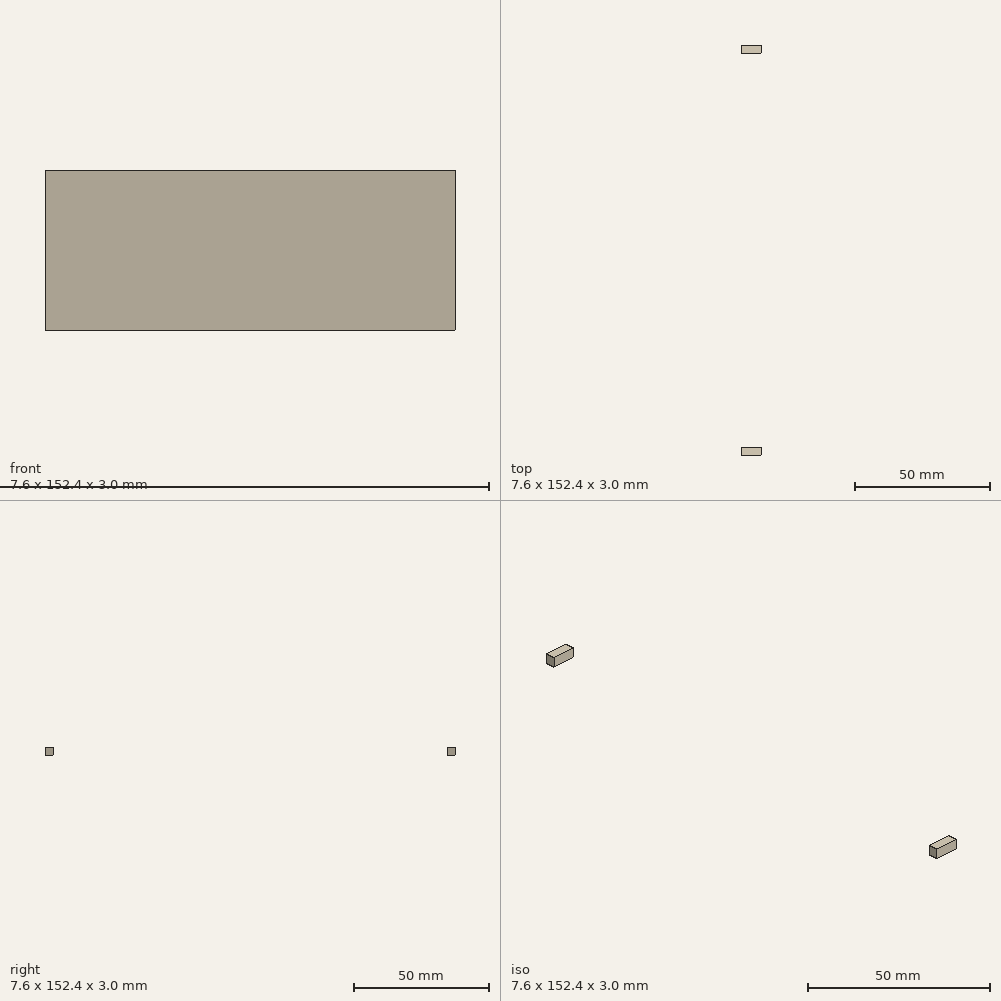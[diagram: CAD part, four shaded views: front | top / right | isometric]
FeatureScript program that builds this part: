
annotation { "Feature Type Name" : "Feature", "Feature Type Description" : "" }
export const myFeature = defineFeature(function(context is Context, id is Id, definition is map)
    precondition{}
    {
        {
            var Q0;
            Q0=qCreatedBy(makeId("Top.planeOp"),FACE);
            var sketch = newSketch(context, id + "F0", { "sketchPlane" : qUnion([Q0])});
            skLineSegment(sketch, "E0.bottom", {"start": v(38.1, -76.2) * mm, "end": v(-38.1, -76.2) * mm});
            skLineSegment(sketch, "E0.top", {"start": v(38.1, 76.2) * mm, "end": v(-38.1, 76.2) * mm});
            skLineSegment(sketch, "E0.left", {"start": v(38.1, -76.2) * mm, "end": v(38.1, 76.2) * mm});
            skLineSegment(sketch, "E0.right", {"start": v(-38.1, -76.2) * mm, "end": v(-38.1, 76.2) * mm});
            skPoint(sketch, "E0.middle", {"position": v(0, 0) * mm});
            skLineSegment(sketch, "E1.bottom", {"start": v(38.1, -73.23) * mm, "end": v(30.48, -73.23) * mm});
            skLineSegment(sketch, "E1.top", {"start": v(38.1, -76.2) * mm, "end": v(30.48, -76.2) * mm});
            skLineSegment(sketch, "E1.left", {"start": v(38.1, -73.23) * mm, "end": v(38.1, -76.2) * mm});
            skLineSegment(sketch, "E1.right", {"start": v(30.48, -73.23) * mm, "end": v(30.48, -76.2) * mm});
            skLineSegment(sketch, "E2.bottom", {"start": v(20.32, -73.23) * mm, "end": v(-25.4, -73.23) * mm});
            skLineSegment(sketch, "E2.top", {"start": v(20.32, -76.2) * mm, "end": v(-25.4, -76.2) * mm});
            skLineSegment(sketch, "E2.left", {"start": v(20.32, -73.23) * mm, "end": v(20.32, -76.2) * mm});
            skLineSegment(sketch, "E2.right", {"start": v(-25.4, -73.23) * mm, "end": v(-25.4, -76.2) * mm});
            skLineSegment(sketch, "E3.bottom", {"start": v(-38.1, -73.23) * mm, "end": v(-35.56, -73.23) * mm});
            skLineSegment(sketch, "E3.top", {"start": v(-38.1, -76.2) * mm, "end": v(-35.56, -76.2) * mm});
            skLineSegment(sketch, "E3.left", {"start": v(-38.1, -73.23) * mm, "end": v(-38.1, -76.2) * mm});
            skLineSegment(sketch, "E3.right", {"start": v(-35.56, -73.23) * mm, "end": v(-35.56, -76.2) * mm});
            skLineSegment(sketch, "E4.MirrorCS", {"start": v(-38.1, 76.2) * mm, "end": v(-35.56, 76.2) * mm});
            skLineSegment(sketch, "E5.MirrorCS", {"start": v(-38.1, 73.23) * mm, "end": v(-38.1, 76.2) * mm});
            skLineSegment(sketch, "E6.MirrorCS", {"start": v(-38.1, 73.23) * mm, "end": v(-35.56, 73.23) * mm});
            skLineSegment(sketch, "E7.MirrorCS", {"start": v(-25.4, 73.23) * mm, "end": v(-25.4, 76.2) * mm});
            skLineSegment(sketch, "E8.MirrorCS", {"start": v(20.32, 73.23) * mm, "end": v(20.32, 76.2) * mm});
            skLineSegment(sketch, "E9.MirrorCS", {"start": v(-35.56, 73.23) * mm, "end": v(-35.56, 76.2) * mm});
            skLineSegment(sketch, "E10.MirrorCS", {"start": v(30.48, 73.23) * mm, "end": v(30.48, 76.2) * mm});
            skLineSegment(sketch, "E11.MirrorCS", {"start": v(38.1, 73.23) * mm, "end": v(38.1, 76.2) * mm});
            skLineSegment(sketch, "E12.MirrorCS", {"start": v(20.32, 76.2) * mm, "end": v(-25.4, 76.2) * mm});
            skLineSegment(sketch, "E13.MirrorCS", {"start": v(20.32, 73.23) * mm, "end": v(-25.4, 73.23) * mm});
            skLineSegment(sketch, "E14.MirrorCS", {"start": v(38.1, 76.2) * mm, "end": v(30.48, 76.2) * mm});
            skLineSegment(sketch, "E15.MirrorCS", {"start": v(38.1, 73.23) * mm, "end": v(30.48, 73.23) * mm});
            skSolve(sketch);
        }
        {
            var Q0;
            Q0=makeQuery(id+"F0.imprint","IMPRINT",FACE,{"disambiguationData":[TD([[makeQuery(id+"F0.imprint","IMPRINT",EDGE,{"derivedFrom":sQuery(id+"F0.wireOp",EDGE,"E0.left")}),1.0]])]});
            extrude(context, id + "F1", {"entities" : qUnion([Q0]), "depth" : 2.97 * mm});
        }
    });
